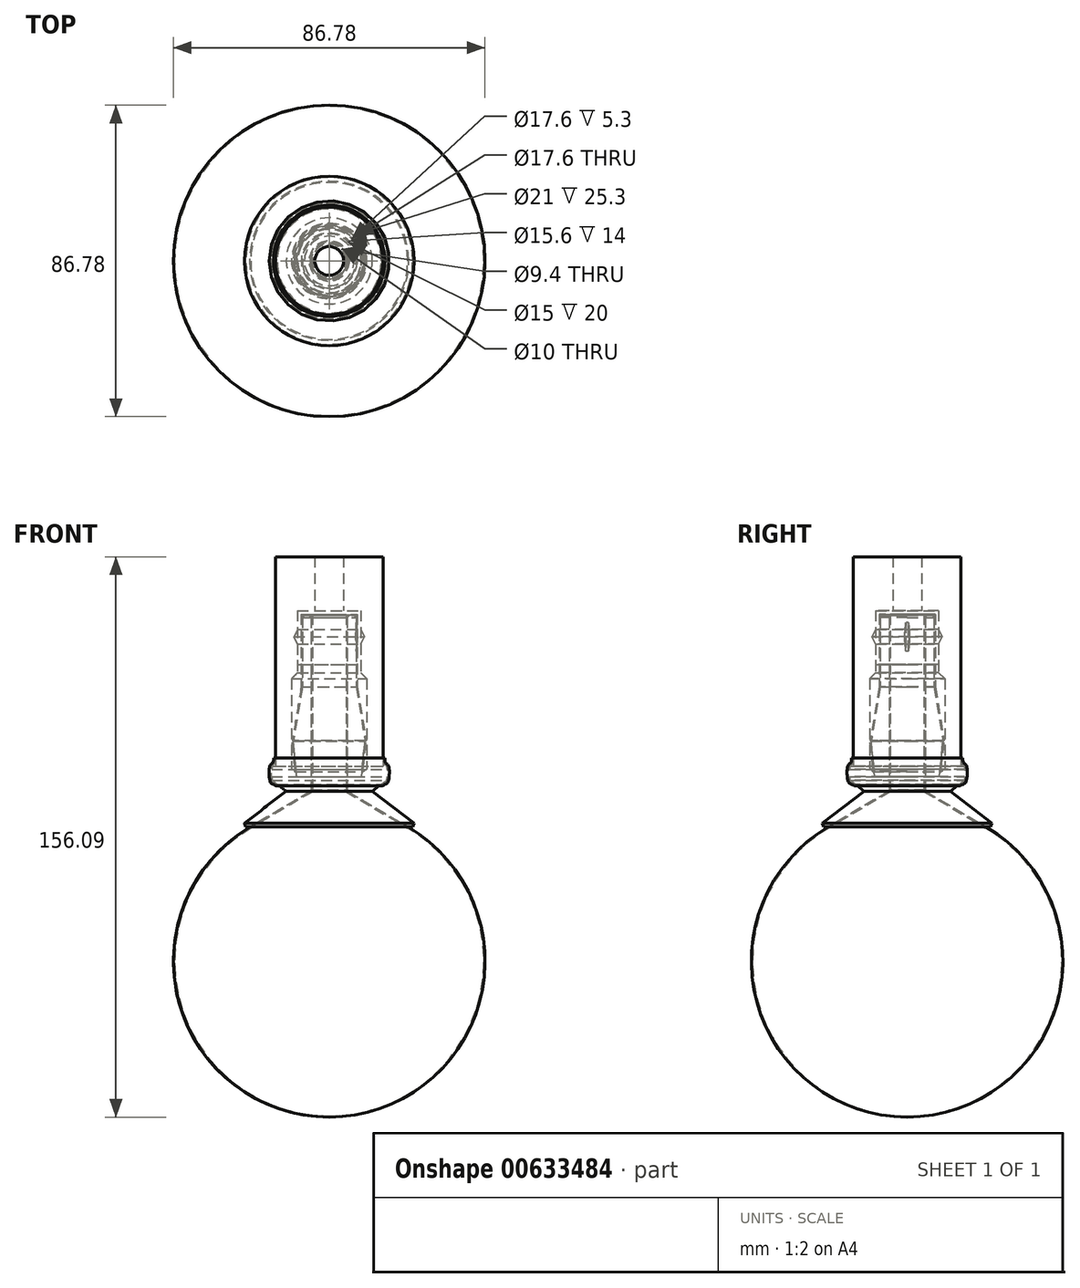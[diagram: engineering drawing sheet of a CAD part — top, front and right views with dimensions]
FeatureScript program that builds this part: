
annotation { "Feature Type Name" : "Feature", "Feature Type Description" : "" }
export const myFeature = defineFeature(function(context is Context, id is Id, definition is map)
    precondition{}
    {
        {
            var Q0;
            Q0=qCreatedBy(makeId("Front.planeOp"),FACE);
            var sketch = newSketch(context, id + "F0", { "sketchPlane" : qUnion([Q0])});
            skLineSegment(sketch, "E0", {"start": v(0, 0) * mm, "end": v(0, 69.42) * mm, "construction": true});
            skLineSegment(sketch, "E1", {"start": v(5, 0) * mm, "end": v(22, -10) * mm});
            skLineSegment(sketch, "E2", {"start": v(22, -10) * mm, "end": v(25, -10) * mm});
            skLineSegment(sketch, "E3", {"start": v(25, -10) * mm, "end": v(12, 0) * mm});
            skLineSegment(sketch, "E4", {"start": v(9, 4) * mm, "end": v(10, 14) * mm});
            skLineSegment(sketch, "E5", {"start": v(10, 14) * mm, "end": v(7.5, 29) * mm});
            skLineSegment(sketch, "E6", {"start": v(7.5, 29) * mm, "end": v(7.5, 49) * mm});
            skLineSegment(sketch, "E7", {"start": v(7.5, 49) * mm, "end": v(5, 49) * mm});
            skLineSegment(sketch, "E8", {"start": v(5, 49) * mm, "end": v(5, 0) * mm});
            skLineSegment(sketch, "E9", {"start": v(7.9, 43) * mm, "end": v(7.5, 39) * mm});
            skLineSegment(sketch, "E10", {"start": v(7.5, 47) * mm, "end": v(7.9, 43) * mm});
            skLineSegment(sketch, "E11", {"start": v(9, 4) * mm, "end": v(16, 4) * mm});
            skLineSegment(sketch, "E12", {"start": v(16, 4) * mm, "end": v(16, 3) * mm});
            skLineSegment(sketch, "E13", {"start": v(16, 3) * mm, "end": v(12, 0) * mm});
            skSolve(sketch);
        }
        {
            var Q0;
            Q0=makeQuery(id+"F0.imprint","IMPRINT",FACE,{"disambiguationData":[TD([[makeQuery(id+"F0.imprint","IMPRINT",EDGE,{"derivedFrom":sQuery(id+"F0.wireOp",EDGE,"E1")}),1.0]])]});
            var Q1;
            Q1=sQuery(id+"F0.wireOp",EDGE,"E0");
            revolve(context, id + "F1", {"entities" : qUnion([Q0]), "axis" : qUnion([Q1]), "revolveType" : RevolveType.FULL});
        }
        {
            var Q0;
            Q0=makeQuery(id+"F1.opRevolve","SWEPT_FACE",FACE,{"disambiguationData":[OSD([sQuery(id+"F0.wireOp",EDGE,"E7")])]});
            var Q1;
            Q1=makeQuery(id+"F1.opRevolve","SWEPT_FACE",FACE,{"disambiguationData":[OSD([sQuery(id+"F0.wireOp",EDGE,"E2")])]});
            var Q2;
            Q2=makeQuery(id+"F1.opRevolve","SWEPT_EDGE",EDGE,{"disambiguationData":[OSD([sQuery(id+"F0.wireOp",EDGE,"E1"),sQuery(id+"F0.wireOp",EDGE,"E8")])]});
            var Q3;
            Q3=makeQuery(id+"F1.opRevolve","SWEPT_EDGE",EDGE,{"disambiguationData":[OSD([sQuery(id+"F0.wireOp",EDGE,"E4"),sQuery(id+"F0.wireOp",EDGE,"E5")])]});
            chamfer(context, id + "F2", {"entities" : qUnion([Q0, Q1, Q2, Q3]), "width" : 0.6 * mm, "tangentPropagation" : true});
        }
        {
            var Q0;
            {var subQ0=sQuery(id+"F0.wireOp",EDGE,"E9");Q0=makeQuery(id+"F0.imprint","IMPRINT",FACE,{"disambiguationData":[TD([[makeQuery(id+"F0.imprint","IMPRINT",EDGE,{"derivedFrom":subQ0}),-1.0]])]});}
            var Q1;
            Q1=sQuery(id+"F0.wireOp",EDGE,"E0");
            revolve(context, id + "F3", {"operationType" : NewBodyOperationType.ADD, "entities" : qUnion([Q0]), "axis" : qUnion([Q1]), "revolveType" : RevolveType.SYMMETRIC, "angle" : 10 * degree});
        }
        {
            var Q0;
            Q0=makeQuery(id+"F3.opRevolve","CAP_EDGE",EDGE,{"disambiguationData":[OSD([sQuery(id+"F0.wireOp",EDGE,"E10")])],"isStart":true});
            var Q1;
            Q1=makeQuery(id+"F3.opRevolve","CAP_EDGE",EDGE,{"disambiguationData":[OSD([sQuery(id+"F0.wireOp",EDGE,"E9")])],"isStart":true});
            var Q2;
            Q2=makeQuery(id+"F3.opRevolve","CAP_EDGE",EDGE,{"disambiguationData":[OSD([sQuery(id+"F0.wireOp",EDGE,"E9")])],"isStart":false});
            var Q3;
            Q3=makeQuery(id+"F3.opRevolve","CAP_EDGE",EDGE,{"disambiguationData":[OSD([sQuery(id+"F0.wireOp",EDGE,"E10")])],"isStart":false});
            var Q4;
            Q4=makeQuery(id+"F3.opRevolve","SWEPT_EDGE",EDGE,{"disambiguationData":[OSD([sQuery(id+"F0.wireOp",EDGE,"E9"),sQuery(id+"F0.wireOp",EDGE,"E10")])]});
            chamfer(context, id + "F4", {"entities" : qUnion([Q0, Q1, Q2, Q3, Q4]), "width" : 0.3 * mm, "tangentPropagation" : true});
        }
        {
            var Q0;
            Q0=qCreatedBy(makeId("Front.planeOp"),FACE);
            var sketch = newSketch(context, id + "F5", { "sketchPlane" : qUnion([Q0])});
            skLineSegment(sketch, "E14", {"start": v(5, 0) * mm, "end": v(22, -10) * mm});
            skLineSegment(sketch, "E15", {"start": v(9.18, 5.78) * mm, "end": v(10, 14) * mm});
            skLineSegment(sketch, "E16", {"start": v(7.5, 29) * mm, "end": v(10, 14) * mm});
            skLineSegment(sketch, "E17", {"start": v(7.5, 29) * mm, "end": v(7.5, 49) * mm});
            skLineSegment(sketch, "E18", {"start": v(7.5, 49) * mm, "end": v(5, 49) * mm});
            skLineSegment(sketch, "E19", {"start": v(5, 49) * mm, "end": v(5, 0) * mm});
            skArc(sketch, "E20", {"start": v(22, -10) * mm, "mid": v(41.87, -58.8) * mm, "end": v(0, -90.8) * mm});
            skArc(sketch, "E21", {"start": v(9.18, 5.78) * mm, "mid": v(9.67, 5.52) * mm, "end": v(9.5, 6.05) * mm});
            skArc(sketch, "E22.0", {"start": v(21.85, -10.26) * mm, "mid": v(41.58, -58.72) * mm, "end": v(0, -90.5) * mm});
            skLineSegment(sketch, "E22.2", {"start": v(7.8, 29.02) * mm, "end": v(10.3, 14) * mm});
            skLineSegment(sketch, "E22.3", {"start": v(9.5, 6.05) * mm, "end": v(10.3, 14) * mm});
            skLineSegment(sketch, "E22.7", {"start": v(7.8, 29.02) * mm, "end": v(7.8, 49.3) * mm});
            skLineSegment(sketch, "E22.8", {"start": v(7.8, 49.3) * mm, "end": v(4.7, 49.3) * mm});
            skLineSegment(sketch, "E22.9", {"start": v(4.7, 49.3) * mm, "end": v(4.7, -0.17) * mm});
            skLineSegment(sketch, "E22.10", {"start": v(4.7, -0.17) * mm, "end": v(21.85, -10.26) * mm});
            skLineSegment(sketch, "E23", {"start": v(0, -90.8) * mm, "end": v(0, -90.5) * mm});
            skSolve(sketch);
        }
        {
            var Q0;
            Q0 = qSketchRegion(id + "F5", true);
            var Q1;
            Q1=sQuery(id+"F0.wireOp",EDGE,"E0");
            revolve(context, id + "F6", {"entities" : qUnion([Q0]), "axis" : qUnion([Q1]), "revolveType" : RevolveType.FULL});
        }
        {
            var Q0;
            Q0=qCreatedBy(makeId("Front.planeOp"),FACE);
            var sketch = newSketch(context, id + "F7", { "sketchPlane" : qUnion([Q0])});
            skLineSegment(sketch, "E24.bottom", {"start": v(0, 50.3) * mm, "end": v(8.8, 50.3) * mm});
            skLineSegment(sketch, "E24.top", {"start": v(0, 49.3) * mm, "end": v(7.8, 49.3) * mm});
            skLineSegment(sketch, "E24.left", {"start": v(0, 50.3) * mm, "end": v(0, 49.3) * mm});
            skLineSegment(sketch, "E25.bottom", {"start": v(8.8, 35.3) * mm, "end": v(7.8, 35.3) * mm});
            skLineSegment(sketch, "E25.left", {"start": v(8.8, 35.3) * mm, "end": v(8.8, 50.3) * mm});
            skLineSegment(sketch, "E25.right", {"start": v(7.8, 35.3) * mm, "end": v(7.8, 49.3) * mm});
            skSolve(sketch);
        }
        {
            var Q0;
            Q0 = qSketchRegion(id + "F7", true);
            var Q1;
            Q1=sQuery(id+"F0.wireOp",EDGE,"E0");
            revolve(context, id + "F8", {"entities" : qUnion([Q0]), "axis" : qUnion([Q1]), "revolveType" : RevolveType.FULL});
        }
        {
            var Q0;
            Q0=qCreatedBy(makeId("Front.planeOp"),FACE);
            var sketch = newSketch(context, id + "F9", { "sketchPlane" : qUnion([Q0])});
            skLineSegment(sketch, "E26", {"start": v(4, 65.3) * mm, "end": v(4, 50.3) * mm});
            skLineSegment(sketch, "E27", {"start": v(4, 50.3) * mm, "end": v(8.8, 50.3) * mm});
            skLineSegment(sketch, "E28", {"start": v(8.8, 50.3) * mm, "end": v(8.8, 45) * mm});
            skLineSegment(sketch, "E29", {"start": v(8.8, 45) * mm, "end": v(9.8, 43) * mm});
            skLineSegment(sketch, "E30", {"start": v(9.8, 43) * mm, "end": v(8.8, 41) * mm});
            skLineSegment(sketch, "E31", {"start": v(8.8, 41) * mm, "end": v(8.8, 33) * mm});
            skLineSegment(sketch, "E32", {"start": v(8.8, 33) * mm, "end": v(10.5, 31.3) * mm});
            skLineSegment(sketch, "E33", {"start": v(10.5, 31.3) * mm, "end": v(10.5, 6) * mm});
            skLineSegment(sketch, "E34", {"start": v(15, 7) * mm, "end": v(15, 65.3) * mm});
            skLineSegment(sketch, "E35", {"start": v(15, 65.3) * mm, "end": v(4, 65.3) * mm});
            skLineSegment(sketch, "E36", {"start": v(0, 0) * mm, "end": v(0, 65.3) * mm, "construction": true});
            skLineSegment(sketch, "E37", {"start": v(10.5, 6) * mm, "end": v(16, 6) * mm});
            skLineSegment(sketch, "E38", {"start": v(16, 6) * mm, "end": v(16, 7) * mm});
            skLineSegment(sketch, "E39", {"start": v(16, 7) * mm, "end": v(15, 7) * mm});
            skSolve(sketch);
        }
        {
            var Q0;
            Q0 = qSketchRegion(id + "F9", true);
            var Q1;
            Q1=sQuery(id+"F9.wireOp",EDGE,"E36");
            revolve(context, id + "F10", {"entities" : qUnion([Q0]), "axis" : qUnion([Q1]), "revolveType" : RevolveType.FULL});
        }
        {
            var Q0;
            Q0=qCreatedBy(makeId("Front.planeOp"),FACE);
            var sketch = newSketch(context, id + "F11", { "sketchPlane" : qUnion([Q0])});
            skFitSpline(sketch, "E40", {"points": [v(15, 9.18) * mm, v(16, 7) * mm, v(16, 3) * mm, v(14.5, 1.88) * mm], "startDerivative": vector(0, -20.76) * mm, "endDerivative": vector(-12.43, -7.81) * mm});
            skFitSpline(sketch, "E41.0", {"points": [v(15.5, 9.18) * mm, v(15.5, 8.77) * mm, v(15.54, 8.32) * mm, v(15.63, 8) * mm, v(15.69, 7.88) * mm, v(15.73, 7.83) * mm, v(15.77, 7.8) * mm, v(15.86, 7.74) * mm, v(16.01, 7.67) * mm, v(16.19, 7.55) * mm, v(16.32, 7.4) * mm, v(16.42, 7.28) * mm, v(16.5, 7.14) * mm, v(16.57, 6.95) * mm, v(16.64, 6.7) * mm, v(16.7, 6.38) * mm, v(16.74, 5.91) * mm, v(16.76, 5.28) * mm, v(16.72, 4.5) * mm, v(16.66, 3.88) * mm, v(16.6, 3.44) * mm, v(16.55, 3.14) * mm, v(16.49, 2.88) * mm, v(16.42, 2.66) * mm, v(16.31, 2.44) * mm, v(16.15, 2.24) * mm, v(15.96, 2.1) * mm, v(15.79, 2.01) * mm, v(15.6, 1.92) * mm, v(15.31, 1.77) * mm, v(15.02, 1.6) * mm, v(14.77, 1.45) * mm]});
            skLineSegment(sketch, "E42", {"start": v(15, 9.18) * mm, "end": v(15.5, 9.18) * mm});
            skLineSegment(sketch, "E43", {"start": v(14.5, 1.88) * mm, "end": v(14.77, 1.45) * mm});
            skSolve(sketch);
        }
        {
            var Q0;
            Q0 = qSketchRegion(id + "F11", true);
            var Q1;
            Q1=sQuery(id+"F0.wireOp",EDGE,"E0");
            revolve(context, id + "F12", {"entities" : qUnion([Q0]), "axis" : qUnion([Q1]), "revolveType" : RevolveType.FULL});
        }
    });
